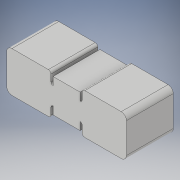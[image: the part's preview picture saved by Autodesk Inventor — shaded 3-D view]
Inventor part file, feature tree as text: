
AUTODESK INVENTOR PART (.ipt)
format: ipt  version: 2018 (Build 220112000, 112)  size: 139,776 bytes
history: native  units: in
note: dims shown in document units (in); Inventor stores cm internally (conversion verified against a paired STEP export)
features: extrude x1, sketch x1
ambient origin geometry x8: Origin, YZ Plane, XZ Plane, XY Plane, X Axis, Y Axis, Z Axis, Center Point
bodies: Solid1 (feature_tree)
feature tree (2):
  extrude  "Extrusion1"  Depth=0.9in
  sketch  "Sketch1"  dims[d0=1.15in d1=0.3in d2=0.04in d3=0.22in d4=0.39in d5=0.32in d6=0.04in d7=0.05in d8=0.1in d9=0.04in d10=0.04in d11=0.9in d12=0.0in]
